# Revit family: Lighting-Linear-Acclaim-Terra
name_source: partatom
category: Lighting Fixtures
units: mm (PartAtom-declared; Revit-internal decimal feet)

## family parameters
Cut with Voids When Loaded = No
Host = Face
Light Source = Yes
Part Type = Normal
Room Calculation Point = No
Round Connector Dimension = Use Diameter
Shared = No

## types (2) — shared parameters
Apparent Load = 0 VA
Color Filter = 16777215
Default Elevation = 1219.2 mm  [stored 4 ft]
Description = Linear
Dimming Lamp Color Temperature Shift = <None>
Emit from Line Length = 609.6 mm  [stored 2 ft]
Housing Finish = Aluminum
Lamp = LED
Manufacturer = Acclaim Lighting
Model = Terra
Number of Poles = 1
Photometric Web File = Load File
Power Factor = 1
Tilt Angle = -90.00°
URL = http://www.acclaimlighting.com
Voltage = 0 V
Width = 73 mm  [stored 0.239501 ft]

## per-type parameters (varying)
| type | Length |
| 305mm | 305 mm  [stored 1.00066 ft] |
| 1220mm | 1220 mm  [stored 4.00262 ft] |

note: [stored X ft] marks values corroborated as IEEE doubles in the binary element streams (Revit-internal decimal feet)

## geometry (parser evidence)
native form markers: Blend x13, Sweep x2
no freeform markers — native parametric forms only
